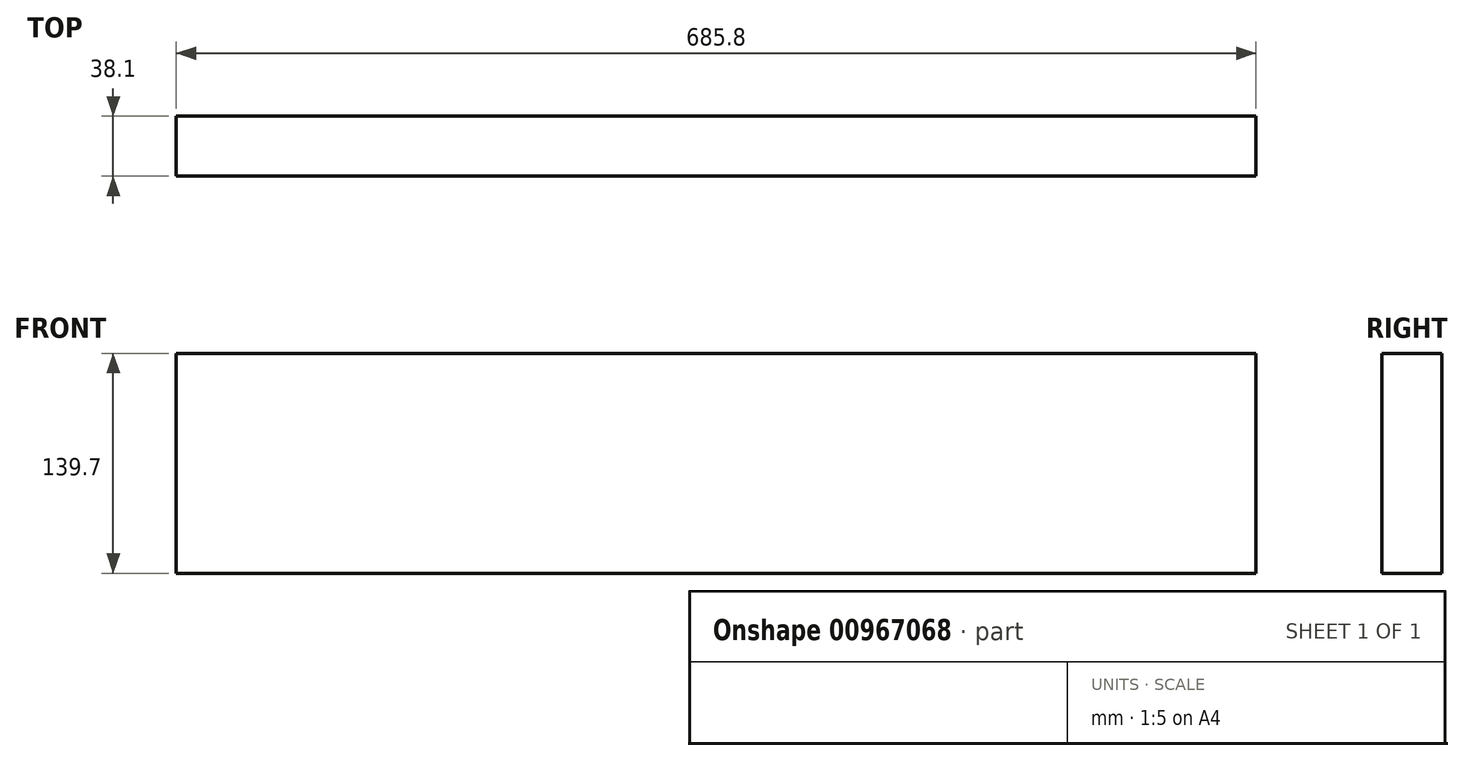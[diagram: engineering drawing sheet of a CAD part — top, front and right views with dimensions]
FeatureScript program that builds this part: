
annotation { "Feature Type Name" : "Feature", "Feature Type Description" : "" }
export const myFeature = defineFeature(function(context is Context, id is Id, definition is map)
    precondition{}
    {
        {
            var Q0;
            Q0=qCreatedBy(makeId("Right.planeOp"),FACE);
            var sketch = newSketch(context, id + "F0", { "sketchPlane" : qUnion([Q0])});
            skLineSegment(sketch, "E0.bottom", {"start": v(0, 0) * mm, "end": v(38.1, 0) * mm});
            skLineSegment(sketch, "E0.top", {"start": v(0, 139.7) * mm, "end": v(38.1, 139.7) * mm});
            skLineSegment(sketch, "E0.left", {"start": v(0, 0) * mm, "end": v(0, 139.7) * mm});
            skLineSegment(sketch, "E0.right", {"start": v(38.1, 0) * mm, "end": v(38.1, 139.7) * mm});
            skSolve(sketch);
        }
        {
            var Q0;
            Q0 = qSketchRegion(id + "F0", true);
            extrude(context, id + "F1", {"entities" : qUnion([Q0]), "oppositeDirection" : true, "depth" : 685.8 * mm, "offsetDistance" : 25.4 * mm});
        }
    });
